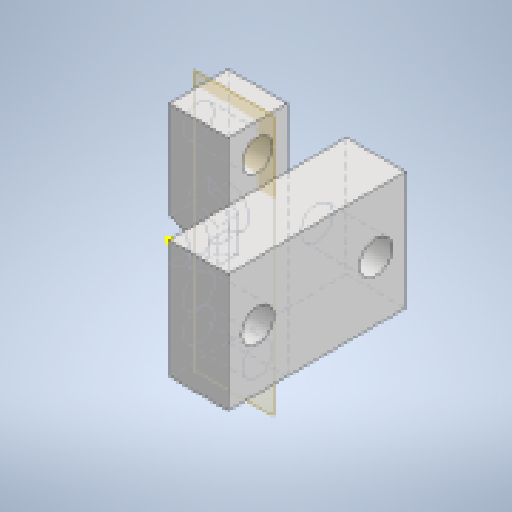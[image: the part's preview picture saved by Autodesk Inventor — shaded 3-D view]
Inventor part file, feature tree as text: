
AUTODESK INVENTOR PART (.ipt)
format: ipt  version: 2023 (Build 270158000, 158)  size: 238,080 bytes
history: native  units: mm
features: sketch x9, extrude x8, plane x1
ambient origin geometry x8: Origin, YZ Plane, XZ Plane, XY Plane, X Axis, Y Axis, Z Axis, Center Point
bodies: Solid1 (feature_tree)
feature tree (18):
  extrude  "Extrusion1"  Depth=20.0mm
  plane  "Work Plane1"
  extrude  "Extrusion2"  Depth=5.0mm
  extrude  "Extrusion3"  Depth=1.8mm
  extrude  "Extrusion4"  Depth=2.5mm
  extrude  "Extrusion5"  Depth=2.5mm
  sketch  "Sketch6"  dims[d21=2.5mm d22=2.6mm]
  extrude  "Extrusion6"  Depth=2.5mm
  extrude  "Extrusion7"  Depth=25.0mm TaperAngle=0.0deg
  extrude  "Extrusion8"  Depth=4.0mm
  sketch  "Sketch1"  dims[d0=20.0mm d1=20.0mm]
  sketch  "Sketch2"  dims[d10=5.0mm d11=0.0mm d12=5.0mm]
  sketch  "Sketch3"  dims[d13=1.8mm d14=0.0mm d15=3.5mm]
  sketch  "Sketch4"  dims[d16=8.0mm d17=0.0mm d18=2.5mm]
  sketch  "Sketch5"  dims[d19=2.5mm d20=2.5mm]
  sketch  "Sketch7"  dims[d23=2.6mm d24=25.0mm d25=0.0mm]
  sketch  "Sketch8"  dims[d26=4.0mm d27=4.0mm]
  sketch  "Sketch9"  dims[d28=4.0mm d29=0.0mm d30=5.0mm d31=5.0mm d32=5.0mm d33=5.0mm d34=10.0mm d35=0.0mm d36=5.0mm d37=5.0mm d38=5.0mm d39=2.75mm d40=2.75mm d41=5.0mm d42=5.0mm d43=5.0mm d44=5.0mm d45=2.5mm d46=2.5mm d47=5.0mm d48=0.0mm d49=4.0mm d50=4.0mm d51=2.0mm d52=0.0mm]
